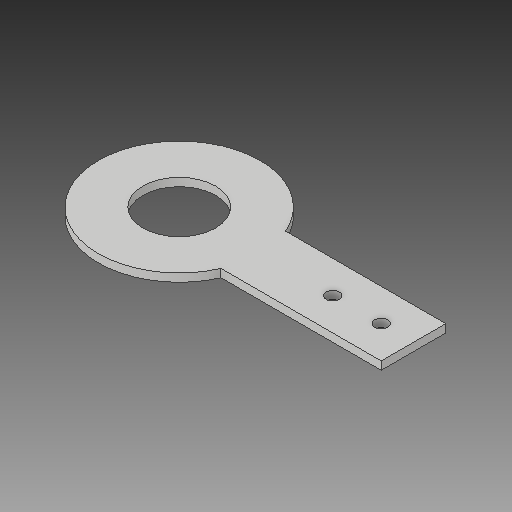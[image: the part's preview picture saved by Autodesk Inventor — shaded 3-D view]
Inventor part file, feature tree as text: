
AUTODESK INVENTOR PART (.ipt)
format: ipt  version: 2018 (Build 220112000, 112)  size: 96,768 bytes
history: native  units: in
note: dims shown in document units (in); Inventor stores cm internally (conversion verified against a paired STEP export)
features: other x3, sketch x1
ambient origin geometry x8: Origin, YZ Plane, XZ Plane, XY Plane, X Axis, Y Axis, Z Axis, Center Point
bodies: Solid1 (feature_tree)
feature tree (4):
  other  "wheel tip_MIR.ipt"
  other  "Solid1::wheel tip_MIR.ipt"
  other  "TaggingFeature1"
  sketch  "Sketch1"  dims[d0=0.3937in]
